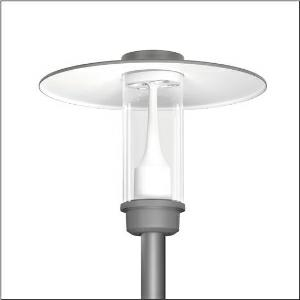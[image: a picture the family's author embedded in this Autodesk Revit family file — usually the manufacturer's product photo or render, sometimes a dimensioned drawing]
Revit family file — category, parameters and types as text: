
# Revit family: litepole_2_iq___p1_0a_5xa5425bf14hp_e9a6
name_source: partatom
category: Lighting Fixtures
units: mm (PartAtom-declared; Revit-internal decimal feet)

## family parameters
Cut with Voids When Loaded = No
Host = Face
Light Source = No
Part Type = Normal
Room Calculation Point = No
Round Connector Dimension = Use Diameter
Shared = No

## types (1)
- --- (1 x LED, 3910 lm, 33.6 W, 2200K)
    Apparent Load = 34 VA
    CIE Flux Codes = 32 62 90 96 100
    Color Rendering = 70
    Color Temperature = 2200K
    Default Elevation = 1800 mm
    Description = Litepole 2 iQ, mast luminaire, Module 540 iQ-SR, primary light control with 3 zone facetted reflector, of plastic, silver coated, highly specular, structured, primary optical cover: cover, of PMMA, transparent, light distribution: P1.0a, light emission: direct distribution, primary light characteristic: strongly asymmetric, installation type: post-top, LED, High Power LED, rated luminous flux: 3.910lm, luminous efficacy: 116lm/W, light colour: 722, colour temperature: 2200K, control gear: iQ Street-Remote, control: pre-setting: logarithmic dimming characteristic, Street-Remote, Auto-Match, Temp-Guard, Lumen-Switch, Night-Set, Smart-Wire, Light-Fading, Desk-Remote (wireless, voltage-free reading and setting of iQ features in the workshop via application-optimized NFC function/RFID function), optimised constant luminous flux control (CLO 2.0), with terminal, 6-pole, max. 2.5mm², mains connection: 230..240V, AC, 50/60Hz, start of lifetime: 34W, end of service life: 36W, reduction: 15W, luminaire housing, upper part, of aluminium, coated, Siteco® metallic grey (DB 702S), diameter: 750mm, height: 590mm, spigot size: d x l = 76 x 70mm (post-top) | with reducer (optional accessory) 60 x 70mm, mounting height: 3..5m, post-top mast mounting element, of diecast aluminium, coated, Siteco® metallic grey (DB 702S), Module 540 iQ-SR, traffic white (RAL 9016), equipment: Power, protection rating (complete): IP65, insulation class (complete): insulation class II (safety insulation), certification: CE, ENEC, VDE, packaging unit: 1 piece

Light Distribution: P1.0a
    Height = 590 mm
    Lamp = 1 x LED
    Lamp Light Flux = 3910 lm
    Lamp Power = 33.6 W
    Lamp count = 1
    Length = 750 mm
    Luminous efficacy = 116 lm/W
    Manufacturer = Siteco
    ModVariant = No
    Model = 5XA5425BF14HP
    Number of Poles = 1
    OnlyDefault = Yes
    Power Factor = 1
    Product Name = Litepole 2 iQ | P1.0a
    Product group = mast luminaire | pylon top
    ProductGroupID = 6100
    Protection Class = Protection class II
    Protection Degree = IP 65
    RLX_Detail_Level = 1
    RLX_Emergency_Light_Flux = 0 lm
    RLX_Emergency_Type = 0
    RLX_Emergency_Type_DB = No
    RlxData = <blob elided: 32061 chars, md5=94eee1fc>
    Socket = socket
    Standby Power = 0 W
    System Light Flux = 3910 lm
    System Power = 34 W
    Type Comments = factory setting: luminous flux: 100 % | dim-lin: 254 | 695 mA
    Type Image = l_1006518.jpg
    URL = http://relux.com
    VarID = @adj_189875
    Voltage = 0 V
    Weight = 0.00 kg
    Width = 0 mm  [stored 0 ft]

note: [stored X ft] marks values corroborated as IEEE doubles in the binary element streams (Revit-internal decimal feet)

## geometry (parser evidence)
native form markers: Blend x4, Sweep x11
no freeform markers — native parametric forms only
